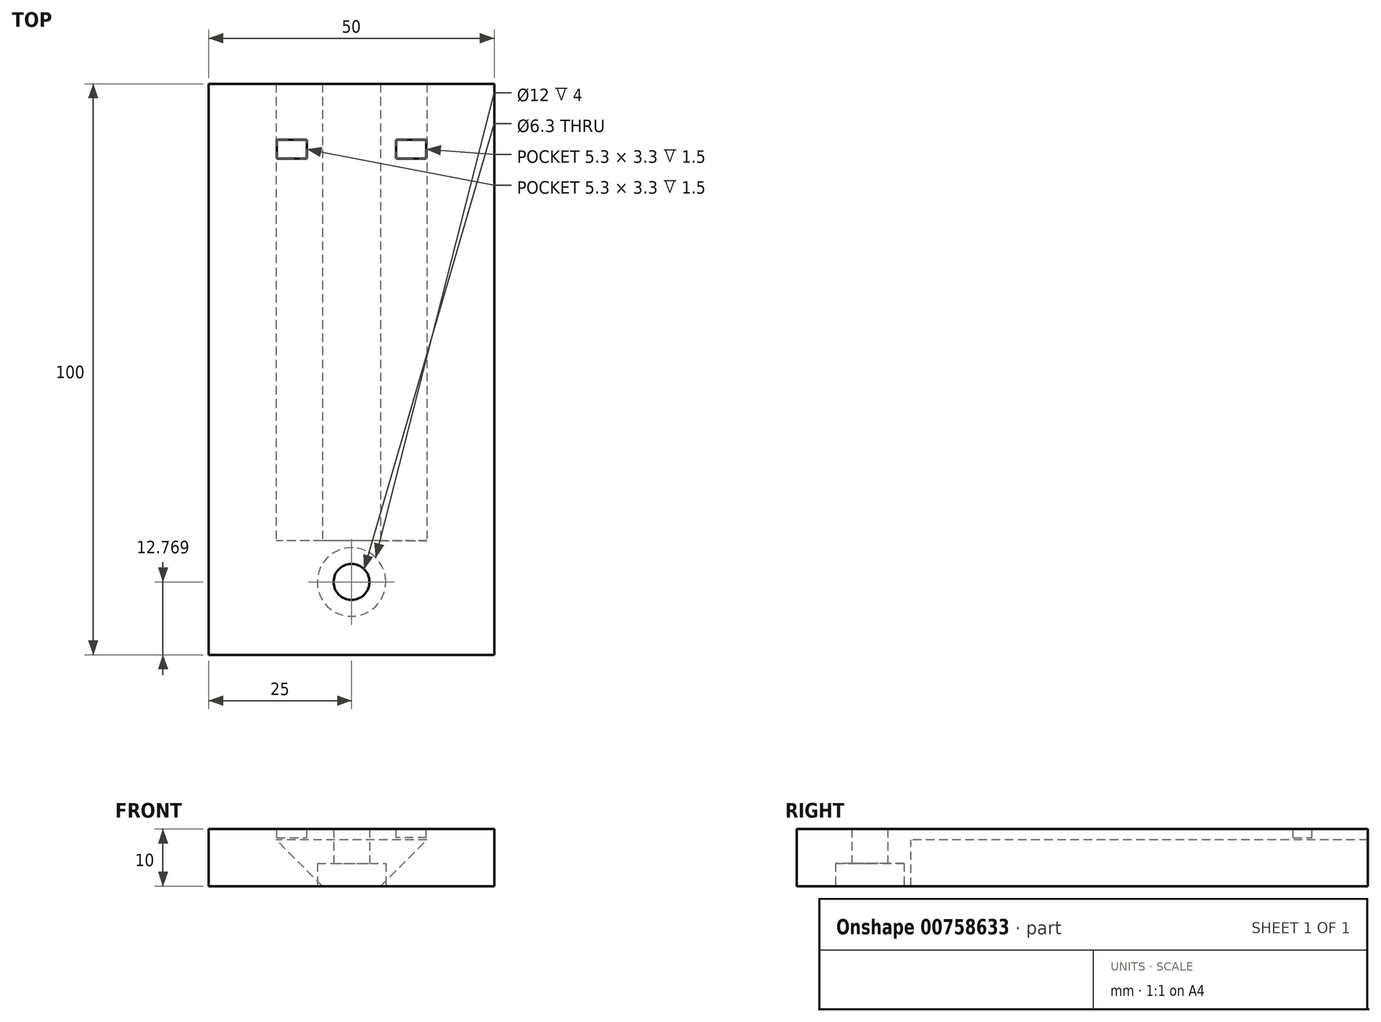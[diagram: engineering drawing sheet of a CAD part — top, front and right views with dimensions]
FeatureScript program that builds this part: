
annotation { "Feature Type Name" : "Feature", "Feature Type Description" : "" }
export const myFeature = defineFeature(function(context is Context, id is Id, definition is map)
    precondition{}
    {
        {
            var Q0;
            Q0=qCreatedBy(makeId("Top.planeOp"),FACE);
            var sketch = newSketch(context, id + "F0", { "sketchPlane" : qUnion([Q0])});
            skLineSegment(sketch, "E0.bottom", {"start": v(25, -50) * mm, "end": v(-25, -50) * mm});
            skLineSegment(sketch, "E0.top", {"start": v(25, 50) * mm, "end": v(-25, 50) * mm});
            skLineSegment(sketch, "E0.left", {"start": v(25, -50) * mm, "end": v(25, 50) * mm});
            skLineSegment(sketch, "E0.right", {"start": v(-25, -50) * mm, "end": v(-25, 50) * mm});
            skPoint(sketch, "E0.middle", {"position": v(0, 0) * mm});
            skSolve(sketch);
        }
        {
            var Q0;
            Q0=makeQuery(id+"F0.imprint","IMPRINT",FACE,{"disambiguationData":[TD([[makeQuery(id+"F0.imprint","IMPRINT",EDGE,{"derivedFrom":sQuery(id+"F0.wireOp",EDGE,"E0.bottom")}),-1.0]])]});
            extrude(context, id + "F1", {"entities" : qUnion([Q0]), "depth" : 10 * mm, "offsetDistance" : 25 * mm});
        }
        {
            var Q0;
            Q0=qCreatedBy(makeId("Front.planeOp"),FACE);
            var sketch = newSketch(context, id + "F2", { "sketchPlane" : qUnion([Q0])});
            skLineSegment(sketch, "E1", {"start": v(0, 0) * mm, "end": v(5.1, 0) * mm});
            skLineSegment(sketch, "E2", {"start": v(5.1, 0) * mm, "end": v(13.2, 8.1) * mm});
            skLineSegment(sketch, "E3", {"start": v(13.2, 8.1) * mm, "end": v(0, 8.1) * mm});
            skLineSegment(sketch, "E4.MirrorCS", {"start": v(-13.2, 8.1) * mm, "end": v(0, 8.1) * mm});
            skLineSegment(sketch, "E5.MirrorCS", {"start": v(-5.1, 0) * mm, "end": v(-13.2, 8.1) * mm});
            skLineSegment(sketch, "E6.MirrorCS", {"start": v(0, 0) * mm, "end": v(-5.1, 0) * mm});
            skSolve(sketch);
        }
        {
            var Q0;
            Q0=makeQuery(id+"F2.imprint","IMPRINT",FACE,{"disambiguationData":[TD([[makeQuery(id+"F2.imprint","IMPRINT",EDGE,{"derivedFrom":sQuery(id+"F2.wireOp",EDGE,"E1")}),1.0]])]});
            extrude(context, id + "F3", {"entities" : qUnion([Q0]), "operationType" : NewBodyOperationType.REMOVE, "oppositeDirection" : true, "depth" : 50 * mm, "offsetDistance" : 25 * mm, "hasSecondDirection" : true, "secondDirectionOppositeDirection" : false, "secondDirectionDepth" : 30 * mm});
        }
        {
            var Q0;
            Q0=makeQuery(id+"F1.opExtrude","CAP_FACE",FACE,{"disambiguationData":[OSD([sQuery(id+"F0.wireOp",EDGE,"E0.bottom"),sQuery(id+"F0.wireOp",EDGE,"E0.top"),sQuery(id+"F0.wireOp",EDGE,"E0.left"),sQuery(id+"F0.wireOp",EDGE,"E0.right")])],"isStart":false});
            var sketch = newSketch(context, id + "F4", { "sketchPlane" : qUnion([Q0])});
            skLineSegment(sketch, "E7.bottom", {"start": v(-13.1, 40.2) * mm, "end": v(-7.8, 40.2) * mm});
            skLineSegment(sketch, "E7.top", {"start": v(-13.1, 36.9) * mm, "end": v(-7.8, 36.9) * mm});
            skLineSegment(sketch, "E7.left", {"start": v(-13.1, 40.2) * mm, "end": v(-13.1, 36.9) * mm});
            skLineSegment(sketch, "E7.right", {"start": v(-7.8, 40.2) * mm, "end": v(-7.8, 36.9) * mm});
            skLineSegment(sketch, "E8.bottom", {"start": v(13.1, 36.9) * mm, "end": v(7.8, 36.9) * mm});
            skLineSegment(sketch, "E8.top", {"start": v(13.1, 40.2) * mm, "end": v(7.8, 40.2) * mm});
            skLineSegment(sketch, "E8.left", {"start": v(13.1, 36.9) * mm, "end": v(13.1, 40.2) * mm});
            skLineSegment(sketch, "E8.right", {"start": v(7.8, 36.9) * mm, "end": v(7.8, 40.2) * mm});
            skSolve(sketch);
        }
        {
            var Q0;
            Q0 = qSketchRegion(id + "F4", true);
            extrude(context, id + "F5", {"entities" : qUnion([Q0]), "operationType" : NewBodyOperationType.REMOVE, "oppositeDirection" : true, "depth" : 1.5 * mm, "offsetDistance" : 25 * mm});
        }
        {
            var Q0;
            Q0=makeQuery(id+"F1.opExtrude","CAP_FACE",FACE,{"disambiguationData":[OSD([sQuery(id+"F0.wireOp",EDGE,"E0.bottom"),sQuery(id+"F0.wireOp",EDGE,"E0.top"),sQuery(id+"F0.wireOp",EDGE,"E0.left"),sQuery(id+"F0.wireOp",EDGE,"E0.right")])],"isStart":true});
            var sketch = newSketch(context, id + "F6", { "sketchPlane" : qUnion([Q0])});
            skCircle(sketch, "E9", {"center": v(0, 37.23) * mm, "radius": 6 * mm});
            skPoint(sketch, "E9.centerSnap0", {"position": v(0, 30) * mm});
            skSolve(sketch);
        }
        {
            var Q0;
            Q0 = qSketchRegion(id + "F6", true);
            extrude(context, id + "F7", {"entities" : qUnion([Q0]), "operationType" : NewBodyOperationType.REMOVE, "oppositeDirection" : true, "depth" : 4 * mm, "offsetDistance" : 25 * mm});
        }
        {
            var Q0;
            Q0=makeQuery(id+"F7.boolean.opBoolean","COPY",FACE,{"derivedFrom":makeQuery(id+"F7.opExtrude","CAP_FACE",FACE,{"disambiguationData":[OSD([sQuery(id+"F6.wireOp",EDGE,"E9")])],"isStart":false})});
            var sketch = newSketch(context, id + "F8", { "sketchPlane" : qUnion([Q0])});
            skCircle(sketch, "E10", {"center": v(0, 37.23) * mm, "radius": 3.15 * mm});
            skSolve(sketch);
        }
        {
            var Q0;
            Q0 = qSketchRegion(id + "F8", true);
            extrude(context, id + "F9", {"entities" : qUnion([Q0]), "operationType" : NewBodyOperationType.REMOVE, "endBound" : BoundingType.UP_TO_NEXT, "oppositeDirection" : true, "depth" : 25 * mm, "offsetDistance" : 25 * mm});
        }
    });
